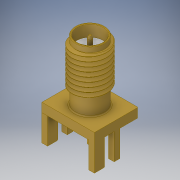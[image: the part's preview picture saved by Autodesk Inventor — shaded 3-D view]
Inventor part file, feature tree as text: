
AUTODESK INVENTOR PART (.ipt)
format: ipt  version: 2019 (Build 230136000, 136)  size: 451,072 bytes
history: native  units: in
note: dims shown in document units (in); Inventor stores cm internally (conversion verified against a paired STEP export)
features: other x2, chamfer x1
ambient origin geometry x8: Origin, YZ Plane, XZ Plane, XY Plane, X Axis, Y Axis, Z Axis, Center Point
bodies: Solid1 (feature_tree), Solid2 (feature_tree), Solid3 (feature_tree)
feature tree (3):
  chamfer  "Chamfer2"  [1 undecoded]
  other  "Boss-Extrude2[1]"
  other  "Boss-Extrude2[2]"
note: 1 required parameter value undecoded (feature->parameter linkage not recoverable at this tier; creation-order binding heuristic only, values carry confidence <= 0.55)
